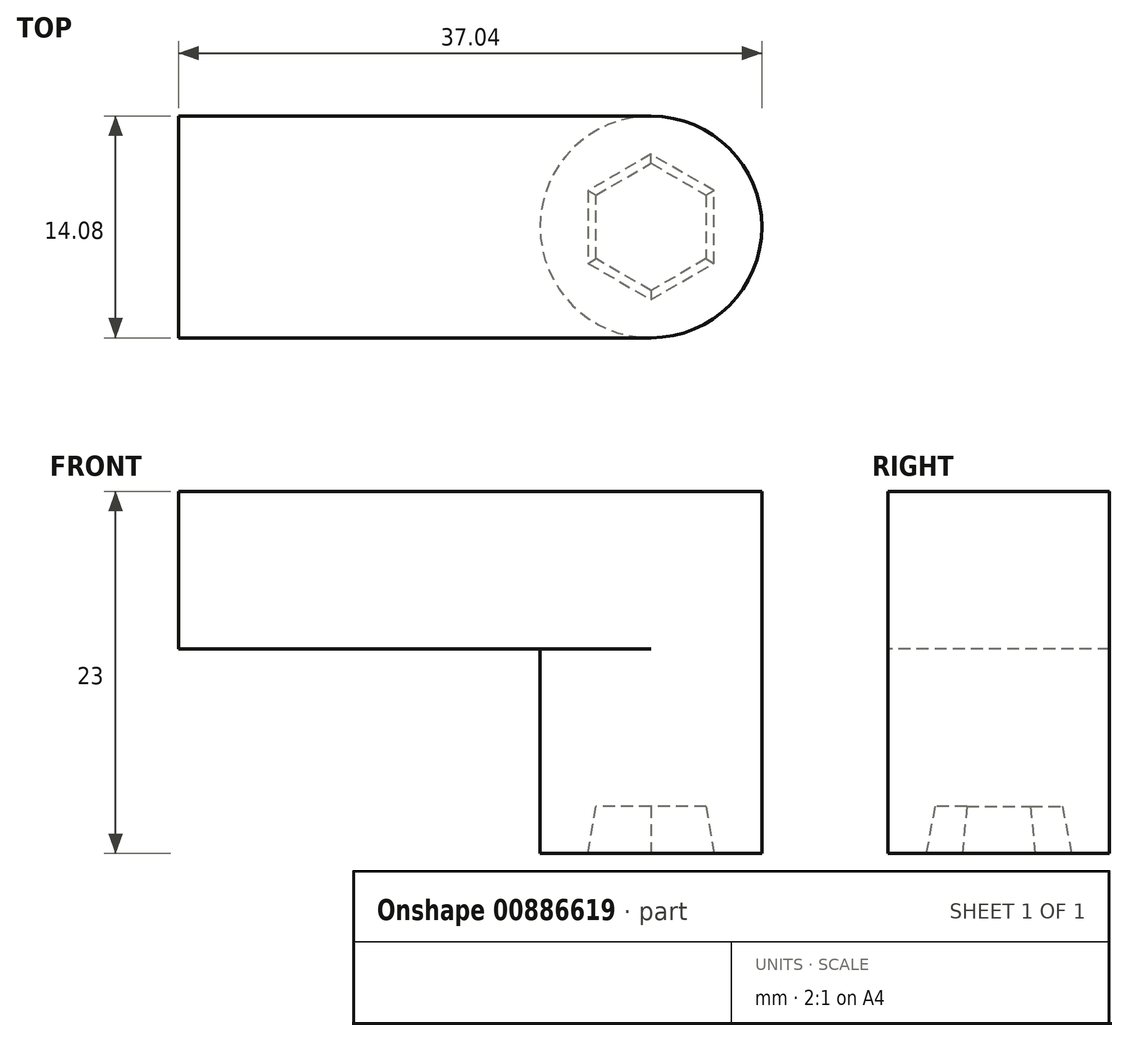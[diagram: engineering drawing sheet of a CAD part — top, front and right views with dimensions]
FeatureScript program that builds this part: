
annotation { "Feature Type Name" : "Feature", "Feature Type Description" : "" }
export const myFeature = defineFeature(function(context is Context, id is Id, definition is map)
    precondition{}
    {
        {
            var Q0;
            Q0=qCreatedBy(makeId("Top.planeOp"),FACE);
            var sketch = newSketch(context, id + "F0", { "sketchPlane" : qUnion([Q0])});
            skCircle(sketch, "E0.cCircle", {"center": v(0, 0) * mm, "radius": 3.5 * mm, "construction": true});
            skLineSegment(sketch, "E0.0", {"start": v(-3.5, -2.02) * mm, "end": v(-3.5, 2.02) * mm});
            skLineSegment(sketch, "E0.1", {"start": v(-3.5, 2.02) * mm, "end": v(0, 4.04) * mm});
            skLineSegment(sketch, "E0.2", {"start": v(0, 4.04) * mm, "end": v(3.5, 2.02) * mm});
            skLineSegment(sketch, "E0.3", {"start": v(3.5, 2.02) * mm, "end": v(3.5, -2.02) * mm});
            skLineSegment(sketch, "E0.4", {"start": v(3.5, -2.02) * mm, "end": v(0, -4.04) * mm});
            skLineSegment(sketch, "E0.5", {"start": v(0, -4.04) * mm, "end": v(-3.5, -2.02) * mm});
            skPoint(sketch, "E0.0.midPoint", {"position": v(-3.5, 0) * mm});
            skCircle(sketch, "E1", {"center": v(0, 0) * mm, "radius": 7.04 * mm});
            skSolve(sketch);
        }
        {
            var Q0;
            Q0=makeQuery(id+"F0.imprint","IMPRINT",FACE,{"disambiguationData":[TD([[makeQuery(id+"F0.imprint","IMPRINT",EDGE,{"derivedFrom":sQuery(id+"F0.wireOp",EDGE,"E0.0")}),1.0]])]});
            extrude(context, id + "F1", {"entities" : qUnion([Q0]), "depth" : 3 * mm, "offsetDistance" : 25 * mm});
        }
        {
            var Q0;
            Q0=makeQuery(id+"F1.opExtrude","CAP_FACE",FACE,{"disambiguationData":[OSD([sQuery(id+"F0.wireOp",EDGE,"E0.0"),sQuery(id+"F0.wireOp",EDGE,"E0.1"),sQuery(id+"F0.wireOp",EDGE,"E0.2"),sQuery(id+"F0.wireOp",EDGE,"E0.3"),sQuery(id+"F0.wireOp",EDGE,"E0.4"),sQuery(id+"F0.wireOp",EDGE,"E0.5"),sQuery(id+"F0.wireOp",EDGE,"E1")])],"isStart":false});
            var sketch = newSketch(context, id + "F2", { "sketchPlane" : qUnion([Q0])});
            skCircle(sketch, "E2", {"center": v(0, 0) * mm, "radius": 7.04 * mm});
            skSolve(sketch);
        }
        {
            var Q0;
            Q0=makeQuery(id+"F2.imprint","IMPRINT",FACE,{"disambiguationData":[TD([[makeQuery(id+"F2.imprint","IMPRINT",EDGE,{"derivedFrom":makeQuery(id+"F1.opExtrude","CAP_EDGE",EDGE,{"disambiguationData":[OSD([sQuery(id+"F0.wireOp",EDGE,"E0.0")])],"isStart":false})}),-1.0]])]});
            var Q1;
            Q1=makeQuery(id+"F2.imprint","IMPRINT",FACE,{"disambiguationData":[TD([[makeQuery(id+"F2.imprint","IMPRINT",EDGE,{"derivedFrom":sQuery(id+"F2.wireOp",EDGE,"E2")}),1.0]])]});
            extrude(context, id + "F3", {"entities" : qUnion([Q0, Q1]), "operationType" : NewBodyOperationType.ADD, "depth" : 10 * mm, "offsetDistance" : 25 * mm});
        }
        {
            var Q0;
            Q0=makeQuery(id+"F3.opExtrude","CAP_FACE",FACE,{"disambiguationData":[OSD([sQuery(id+"F2.wireOp",EDGE,"E2")])],"isStart":false});
            var sketch = newSketch(context, id + "F4", { "sketchPlane" : qUnion([Q0])});
            skLineSegment(sketch, "E3", {"start": v(0, 7.04) * mm, "end": v(-30, 7.04) * mm});
            skLineSegment(sketch, "E4", {"start": v(-30, 7.04) * mm, "end": v(-30, -7.04) * mm});
            skLineSegment(sketch, "E5", {"start": v(-30, -7.04) * mm, "end": v(0, -7.04) * mm});
            skSolve(sketch);
        }
        {
            var Q0;
            {var subQ0=makeQuery(id+"F3.opExtrude","CAP_EDGE",EDGE,{"disambiguationData":[OSD([sQuery(id+"F2.wireOp",EDGE,"E2")])],"isStart":false});var subQ1=makeQuery(id+"F4.imprint","INTERSECT",VERTEX,{"derivedFrom":[subQ0,sQuery(id+"F4.wireOp",EDGE,"E3")]});Q0=makeQuery(id+"F4.imprint","IMPRINT",FACE,{"disambiguationData":[TD([[makeQuery(id+"F4.imprint","IMPRINT",EDGE,{"disambiguationData":[TD([[subQ1,1.0]])],"derivedFrom":subQ0}),1.0]])]});}
            var Q1;
            {var subQ0=sQuery(id+"F4.wireOp",EDGE,"E3");Q1=makeQuery(id+"F4.imprint","IMPRINT",FACE,{"disambiguationData":[TD([[makeQuery(id+"F4.imprint","IMPRINT",EDGE,{"derivedFrom":subQ0}),1.0]])]});}
            extrude(context, id + "F5", {"entities" : qUnion([Q0, Q1]), "operationType" : NewBodyOperationType.ADD, "depth" : 10 * mm, "offsetDistance" : 25 * mm});
        }
        {
            var Q0;
            Q0=makeQuery(id+"F1.opExtrude","CAP_EDGE",EDGE,{"disambiguationData":[OSD([sQuery(id+"F0.wireOp",EDGE,"E0.5")])],"isStart":true});
            var Q1;
            Q1=makeQuery(id+"F1.opExtrude","CAP_EDGE",EDGE,{"disambiguationData":[OSD([sQuery(id+"F0.wireOp",EDGE,"E0.0")])],"isStart":true});
            var Q2;
            Q2=makeQuery(id+"F1.opExtrude","CAP_EDGE",EDGE,{"disambiguationData":[OSD([sQuery(id+"F0.wireOp",EDGE,"E0.4")])],"isStart":true});
            var Q3;
            Q3=makeQuery(id+"F1.opExtrude","CAP_EDGE",EDGE,{"disambiguationData":[OSD([sQuery(id+"F0.wireOp",EDGE,"E0.3")])],"isStart":true});
            var Q4;
            Q4=makeQuery(id+"F1.opExtrude","CAP_EDGE",EDGE,{"disambiguationData":[OSD([sQuery(id+"F0.wireOp",EDGE,"E0.2")])],"isStart":true});
            var Q5;
            Q5=makeQuery(id+"F1.opExtrude","CAP_EDGE",EDGE,{"disambiguationData":[OSD([sQuery(id+"F0.wireOp",EDGE,"E0.1")])],"isStart":true});
            chamfer(context, id + "F6", {"entities" : qUnion([Q0, Q1, Q2, Q3, Q4, Q5]), "chamferType" : ChamferType.TWO_OFFSETS, "width1" : 3 * mm, "oppositeDirection" : false, "width2" : 0.5 * mm, "tangentPropagation" : true});
        }
    });
